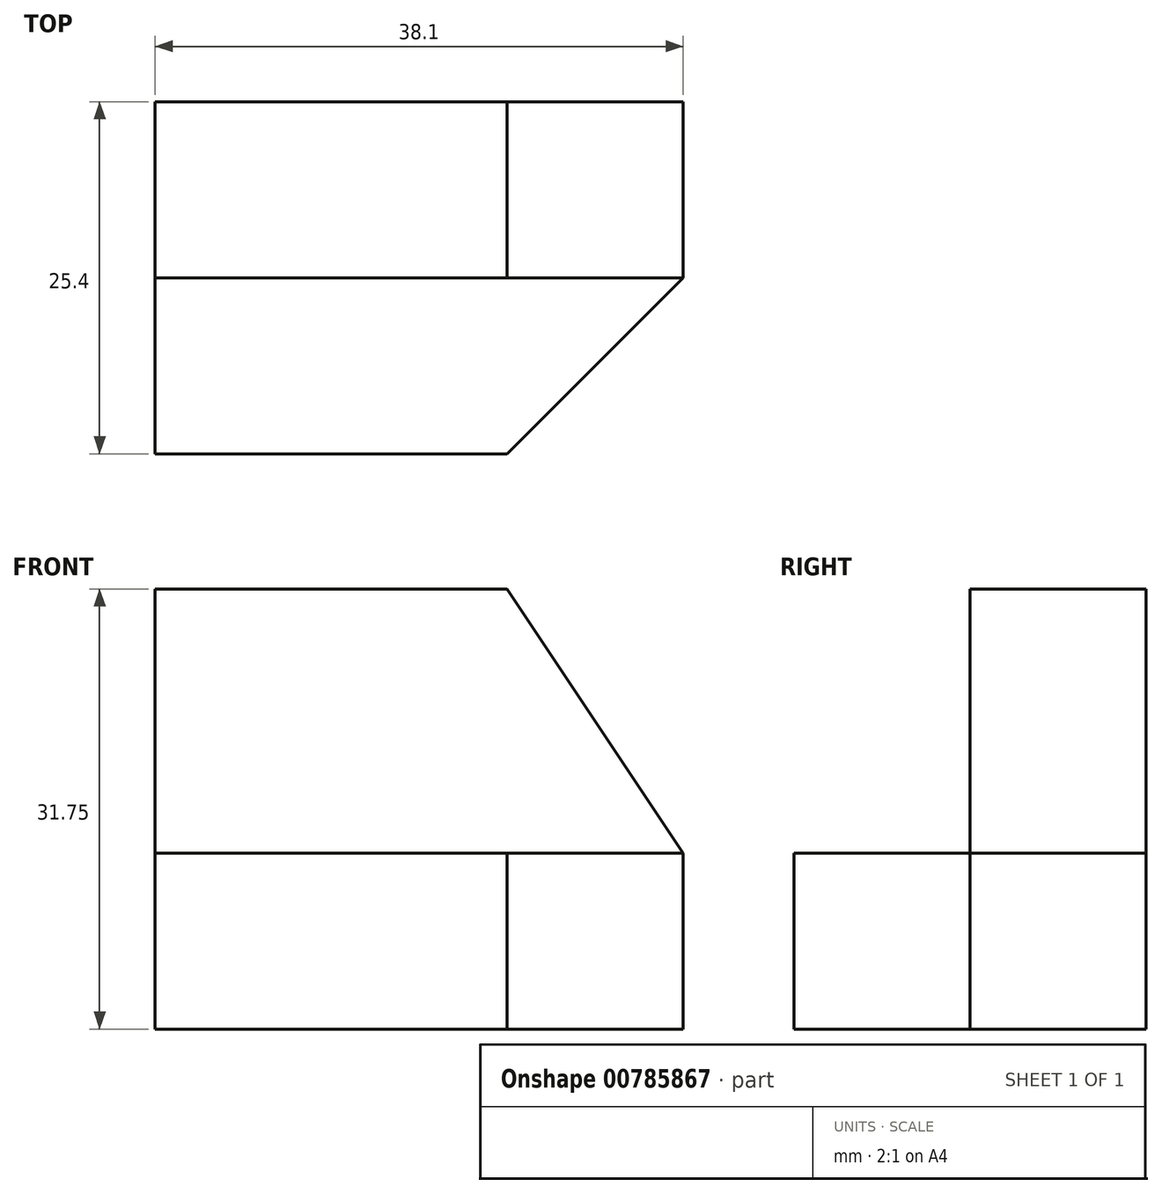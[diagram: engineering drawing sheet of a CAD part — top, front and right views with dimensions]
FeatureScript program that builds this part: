
annotation { "Feature Type Name" : "Feature", "Feature Type Description" : "" }
export const myFeature = defineFeature(function(context is Context, id is Id, definition is map)
    precondition{}
    {
        {
            var Q0;
            Q0=qCreatedBy(makeId("Front.planeOp"),FACE);
            var sketch = newSketch(context, id + "F0", { "sketchPlane" : qUnion([Q0])});
            skLineSegment(sketch, "E0", {"start": v(0, 0) * mm, "end": v(38.1, 0) * mm});
            skLineSegment(sketch, "E1", {"start": v(0, 0) * mm, "end": v(0, 31.75) * mm});
            skLineSegment(sketch, "E2", {"start": v(0, 31.75) * mm, "end": v(38.1, 31.75) * mm});
            skLineSegment(sketch, "E3", {"start": v(38.1, 31.75) * mm, "end": v(38.1, 0) * mm});
            skSolve(sketch);
        }
        {
            var Q0;
            Q0=makeQuery(id+"F0.imprint","IMPRINT",FACE,{"disambiguationData":[TD([[makeQuery(id+"F0.imprint","IMPRINT",EDGE,{"derivedFrom":sQuery(id+"F0.wireOp",EDGE,"E0")}),1.0]])]});
            extrude(context, id + "F1", {"entities" : qUnion([Q0]), "depth" : 25.4 * mm, "offsetDistance" : 25.4 * mm});
        }
        {
            var Q0;
            Q0=makeQuery(id+"F1.opExtrude","CAP_FACE",FACE,{"disambiguationData":[OSD([sQuery(id+"F0.wireOp",EDGE,"E0"),sQuery(id+"F0.wireOp",EDGE,"E1"),sQuery(id+"F0.wireOp",EDGE,"E2"),sQuery(id+"F0.wireOp",EDGE,"E3")])],"isStart":false});
            var sketch = newSketch(context, id + "F2", { "sketchPlane" : qUnion([Q0])});
            skLineSegment(sketch, "E4", {"start": v(0, 0) * mm, "end": v(0, 12.7) * mm});
            skLineSegment(sketch, "E5", {"start": v(0, 12.7) * mm, "end": v(25.4, 12.7) * mm});
            skLineSegment(sketch, "E6", {"start": v(25.4, 12.7) * mm, "end": v(25.4, 0) * mm});
            skLineSegment(sketch, "E7", {"start": v(25.4, 12.7) * mm, "end": v(25.4, 31.75) * mm});
            skLineSegment(sketch, "E8", {"start": v(0, 12.7) * mm, "end": v(0, 31.75) * mm});
            skLineSegment(sketch, "E9", {"start": v(0, 31.75) * mm, "end": v(25.4, 31.75) * mm});
            skSolve(sketch);
        }
        {
            var Q0;
            Q0=makeQuery(id+"F2.imprint","IMPRINT",FACE,{"disambiguationData":[TD([[makeQuery(id+"F2.imprint","IMPRINT",EDGE,{"derivedFrom":sQuery(id+"F2.wireOp",EDGE,"E5")}),1.0]])]});
            extrude(context, id + "F3", {"entities" : qUnion([Q0]), "operationType" : NewBodyOperationType.REMOVE, "oppositeDirection" : true, "depth" : 12.7 * mm, "offsetDistance" : 25.4 * mm});
        }
        {
            var Q0;
            Q0=makeQuery(id+"F1.opExtrude","CAP_FACE",FACE,{"disambiguationData":[OSD([sQuery(id+"F0.wireOp",EDGE,"E0"),sQuery(id+"F0.wireOp",EDGE,"E1"),sQuery(id+"F0.wireOp",EDGE,"E2"),sQuery(id+"F0.wireOp",EDGE,"E3")])],"isStart":false});
            var sketch = newSketch(context, id + "F4", { "sketchPlane" : qUnion([Q0])});
            skLineSegment(sketch, "E10", {"start": v(25.4, 12.7) * mm, "end": v(38.1, 12.7) * mm});
            skSolve(sketch);
        }
        {
            var Q0;
            {var subQ0=sQuery(id+"F4.wireOp",EDGE,"E10");Q0=makeQuery(id+"F4.imprint","IMPRINT",FACE,{"disambiguationData":[TD([[makeQuery(id+"F4.imprint","IMPRINT",EDGE,{"derivedFrom":subQ0}),1.0]])]});}
            extrude(context, id + "F5", {"entities" : qUnion([Q0]), "operationType" : NewBodyOperationType.REMOVE, "oppositeDirection" : true, "depth" : 12.7 * mm, "offsetDistance" : 25.4 * mm});
        }
        {
            var Q0;
            Q0=makeQuery(id+"F5.boolean.opBoolean","MERGE",FACE,{"derivedFrom":[makeQuery(id+"F3.boolean.opBoolean","COPY",FACE,{"derivedFrom":makeQuery(id+"F3.opExtrude","SWEPT_FACE",FACE,{"disambiguationData":[OSD([sQuery(id+"F2.wireOp",EDGE,"E5")])]})}),makeQuery(id+"F5.opExtrude","SWEPT_FACE",FACE,{"disambiguationData":[OSD([sQuery(id+"F4.wireOp",EDGE,"E10")])]})]});
            var sketch = newSketch(context, id + "F6", { "sketchPlane" : qUnion([Q0])});
            skLineSegment(sketch, "E11", {"start": v(0, -25.4) * mm, "end": v(25.4, -25.4) * mm});
            skLineSegment(sketch, "E12", {"start": v(25.4, -25.4) * mm, "end": v(38.1, -12.7) * mm});
            skLineSegment(sketch, "E13", {"start": v(25.4, -25.4) * mm, "end": v(38.1, -38.1) * mm});
            skLineSegment(sketch, "E14", {"start": v(38.1, -12.7) * mm, "end": v(50.8, -25.4) * mm});
            skSolve(sketch);
        }
        {
            var Q0;
            {var subQ0=sQuery(id+"F6.wireOp",EDGE,"E12");Q0=makeQuery(id+"F6.imprint","IMPRINT",FACE,{"disambiguationData":[TD([[makeQuery(id+"F6.imprint","IMPRINT",EDGE,{"derivedFrom":subQ0}),-1.0]])]});}
            extrude(context, id + "F7", {"entities" : qUnion([Q0]), "operationType" : NewBodyOperationType.REMOVE, "oppositeDirection" : true, "depth" : 25.4 * mm, "offsetDistance" : 25.4 * mm});
        }
        {
            var Q0;
            {var subQ0=sQuery(id+"F2.wireOp",EDGE,"E7");Q0=makeQuery(id+"F5.boolean.opBoolean","MERGE",FACE,{"derivedFrom":[makeQuery(id+"F3.boolean.opBoolean","COPY",FACE,{"derivedFrom":makeQuery(id+"F3.opExtrude","CAP_FACE",FACE,{"disambiguationData":[OSD([sQuery(id+"F2.wireOp",EDGE,"E5"),subQ0,sQuery(id+"F2.wireOp",EDGE,"E8"),sQuery(id+"F2.wireOp",EDGE,"E9")])],"isStart":false})}),makeQuery(id+"F5.opExtrude","CAP_FACE",FACE,{"disambiguationData":[OSD([sQuery(id+"F0.wireOp",EDGE,"E2"),sQuery(id+"F0.wireOp",EDGE,"E3"),subQ0,sQuery(id+"F4.wireOp",EDGE,"E10")])],"isStart":false})]});}
            var sketch = newSketch(context, id + "F8", { "sketchPlane" : qUnion([Q0])});
            skLineSegment(sketch, "E15", {"start": v(38.1, 31.75) * mm, "end": v(25.4, 31.75) * mm});
            skLineSegment(sketch, "E16", {"start": v(25.4, 31.75) * mm, "end": v(38.1, 12.7) * mm});
            skSolve(sketch);
        }
        {
            var Q0;
            Q0=makeQuery(id+"F8.imprint","IMPRINT",FACE,{"disambiguationData":[TD([[makeQuery(id+"F8.imprint","IMPRINT",EDGE,{"derivedFrom":sQuery(id+"F8.wireOp",EDGE,"E15")}),-1.0]])]});
            extrude(context, id + "F9", {"entities" : qUnion([Q0]), "operationType" : NewBodyOperationType.REMOVE, "oppositeDirection" : true, "depth" : 25.4 * mm, "offsetDistance" : 25.4 * mm});
        }
    });
